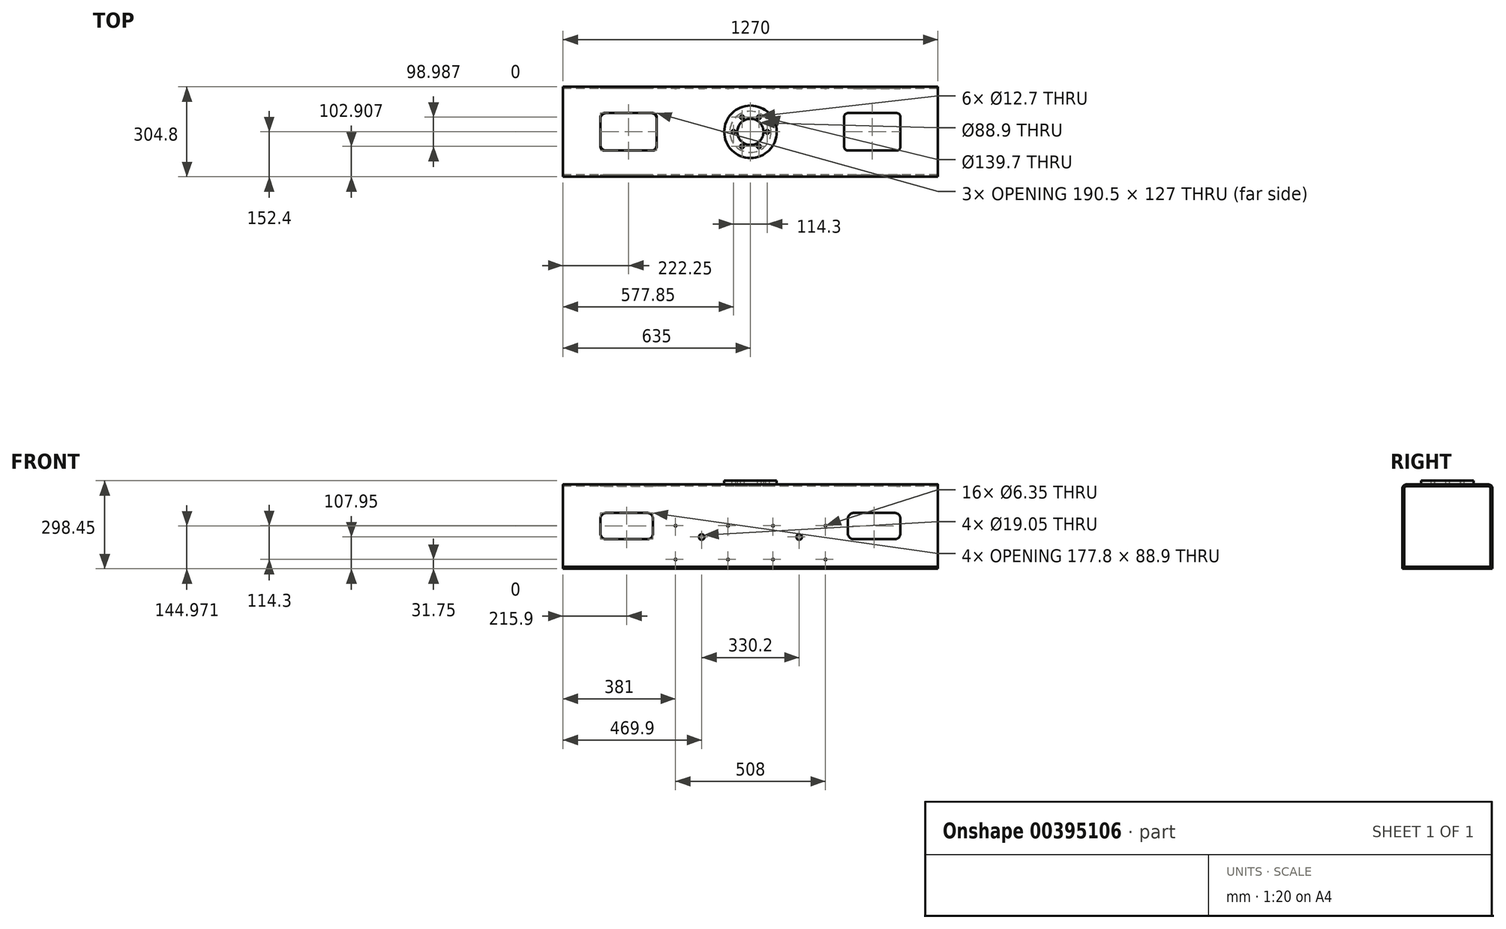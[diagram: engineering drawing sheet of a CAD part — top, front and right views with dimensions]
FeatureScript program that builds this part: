
annotation { "Feature Type Name" : "Feature", "Feature Type Description" : "" }
export const myFeature = defineFeature(function(context is Context, id is Id, definition is map)
    precondition{}
    {
        {
            var Q0;
            Q0=qCreatedBy(makeId("Right.planeOp"),FACE);
            var sketch = newSketch(context, id + "F0", { "sketchPlane" : qUnion([Q0])});
            skLineSegment(sketch, "E0.bottom", {"start": v(-139.7, 139.7) * mm, "end": v(139.7, 139.7) * mm});
            skLineSegment(sketch, "E0.top", {"start": v(-152.4, -139.7) * mm, "end": v(152.4, -139.7) * mm, "construction": true});
            skLineSegment(sketch, "E0.left", {"start": v(-152.4, 127) * mm, "end": v(-152.4, -139.7) * mm});
            skLineSegment(sketch, "E0.right", {"start": v(152.4, 127) * mm, "end": v(152.4, -139.7) * mm});
            skPoint(sketch, "E0.middle", {"position": v(0, 0) * mm});
            skLineSegment(sketch, "E1", {"start": v(-152.4, -139.7) * mm, "end": v(-146.05, -139.7) * mm});
            skLineSegment(sketch, "E2", {"start": v(146.05, -139.7) * mm, "end": v(152.4, -139.7) * mm});
            skPoint(sketch, "E3.visualSharp", {"position": v(-152.4, 139.7) * mm});
            skArc(sketch, "E3.filletArc", {"start": v(-139.7, 139.7) * mm, "mid": v(-148.68, 135.98) * mm, "end": v(-152.4, 127) * mm});
            skPoint(sketch, "E4.visualSharp", {"position": v(152.4, 139.7) * mm});
            skArc(sketch, "E4.filletArc", {"start": v(152.4, 127) * mm, "mid": v(148.68, 135.98) * mm, "end": v(139.7, 139.7) * mm});
            skLineSegment(sketch, "E5.0", {"start": v(-146.05, 127) * mm, "end": v(-146.05, -139.7) * mm});
            skArc(sketch, "E5.1", {"start": v(-139.7, 133.35) * mm, "mid": v(-144.2, 131.5) * mm, "end": v(-146.05, 127) * mm});
            skLineSegment(sketch, "E6.0", {"start": v(146.05, 127) * mm, "end": v(146.05, -139.7) * mm});
            skArc(sketch, "E6.1", {"start": v(146.05, 127) * mm, "mid": v(144.2, 131.5) * mm, "end": v(139.7, 133.35) * mm});
            skLineSegment(sketch, "E6.2", {"start": v(-139.7, 133.35) * mm, "end": v(139.7, 133.35) * mm});
            skSolve(sketch);
        }
        {
            var Q0;
            Q0 = qSketchRegion(id + "F0", true);
            extrude(context, id + "F1", {"entities" : qUnion([Q0]), "depth" : 1270 * mm});
        }
        {
            var Q0;
            Q0=makeQuery(id+"F1.opExtrude","SWEPT_FACE",FACE,{"disambiguationData":[OSD([sQuery(id+"F0.wireOp",EDGE,"E0.bottom")])]});
            var sketch = newSketch(context, id + "F2", { "sketchPlane" : qUnion([Q0])});
            skLineSegment(sketch, "E7", {"start": v(635, -139.7) * mm, "end": v(635, 139.7) * mm, "construction": true});
            skLineSegment(sketch, "E8.bottom", {"start": v(139.7, 63.5) * mm, "end": v(304.8, 63.5) * mm});
            skLineSegment(sketch, "E8.top", {"start": v(139.7, -63.5) * mm, "end": v(304.8, -63.5) * mm});
            skLineSegment(sketch, "E8.left", {"start": v(127, 50.8) * mm, "end": v(127, -50.8) * mm});
            skLineSegment(sketch, "E8.right", {"start": v(317.5, 50.8) * mm, "end": v(317.5, -50.8) * mm});
            skPoint(sketch, "E9.visualSharp", {"position": v(127, 63.5) * mm});
            skArc(sketch, "E9.filletArc", {"start": v(139.7, 63.5) * mm, "mid": v(130.72, 59.78) * mm, "end": v(127, 50.8) * mm});
            skPoint(sketch, "E10.visualSharp", {"position": v(317.5, 63.5) * mm});
            skArc(sketch, "E10.filletArc", {"start": v(317.5, 50.8) * mm, "mid": v(313.78, 59.78) * mm, "end": v(304.8, 63.5) * mm});
            skPoint(sketch, "E11.visualSharp", {"position": v(317.5, -63.5) * mm});
            skArc(sketch, "E11.filletArc", {"start": v(304.8, -63.5) * mm, "mid": v(313.78, -59.78) * mm, "end": v(317.5, -50.8) * mm});
            skPoint(sketch, "E12.visualSharp", {"position": v(127, -63.5) * mm});
            skArc(sketch, "E12.filletArc", {"start": v(127, -50.8) * mm, "mid": v(130.72, -59.78) * mm, "end": v(139.7, -63.5) * mm});
            skPoint(sketch, "E13.endSnap0", {"position": v(317.5, 0) * mm});
            skPoint(sketch, "E14.trimOffspring.end.orphan", {"position": v(3692.39, 0) * mm});
            skPoint(sketch, "E15.orphan", {"position": v(0, 0) * mm});
            skLineSegment(sketch, "E16.0", {"start": v(0, -139.7) * mm, "end": v(0, 139.7) * mm});
            skLineSegment(sketch, "E17.0", {"start": v(1270, -139.7) * mm, "end": v(1270, 139.7) * mm});
            skLineSegment(sketch, "E18", {"start": v(3692.39, 0) * mm, "end": v(0, 0) * mm, "construction": true});
            skPoint(sketch, "E19", {"position": v(127, 0) * mm});
            skLineSegment(sketch, "E20.MirrorCS", {"start": v(1130.3, -63.5) * mm, "end": v(965.2, -63.5) * mm});
            skArc(sketch, "E21.MirrorCS", {"start": v(965.2, -63.5) * mm, "mid": v(956.22, -59.78) * mm, "end": v(952.5, -50.8) * mm});
            skLineSegment(sketch, "E22.MirrorCS", {"start": v(952.5, 50.8) * mm, "end": v(952.5, -50.8) * mm});
            skArc(sketch, "E23.MirrorCS", {"start": v(952.5, 50.8) * mm, "mid": v(956.22, 59.78) * mm, "end": v(965.2, 63.5) * mm});
            skLineSegment(sketch, "E24.MirrorCS", {"start": v(1130.3, 63.5) * mm, "end": v(965.2, 63.5) * mm});
            skLineSegment(sketch, "E25.MirrorCS", {"start": v(1143, 50.8) * mm, "end": v(1143, -50.8) * mm});
            skArc(sketch, "E26.MirrorCS", {"start": v(1130.3, 63.5) * mm, "mid": v(1139.28, 59.78) * mm, "end": v(1143, 50.8) * mm});
            skArc(sketch, "E27.MirrorCS", {"start": v(1143, -50.8) * mm, "mid": v(1139.28, -59.78) * mm, "end": v(1130.3, -63.5) * mm});
            skCircle(sketch, "E28", {"center": v(635, 0) * mm, "radius": 69.85 * mm});
            skSolve(sketch);
        }
        {
            var Q0;
            Q0 = qSketchRegion(id + "F2", true);
            extrude(context, id + "F3", {"entities" : qUnion([Q0]), "operationType" : NewBodyOperationType.REMOVE, "endBound" : BoundingType.THROUGH_ALL, "oppositeDirection" : true, "depth" : 25.4 * mm});
        }
        {
            var Q0;
            Q0=makeQuery(id+"F1.opExtrude","SWEPT_FACE",FACE,{"disambiguationData":[OSD([sQuery(id+"F0.wireOp",EDGE,"E0.left")])]});
            var sketch = newSketch(context, id + "F4", { "sketchPlane" : qUnion([Q0])});
            skLineSegment(sketch, "E29", {"start": v(0, 0) * mm, "end": v(1270, -6.35) * mm, "construction": true});
            skLineSegment(sketch, "E30.bottom", {"start": v(146.05, 43.37) * mm, "end": v(285.75, 43.37) * mm});
            skLineSegment(sketch, "E30.top", {"start": v(146.05, -45.53) * mm, "end": v(285.75, -45.53) * mm});
            skLineSegment(sketch, "E30.left", {"start": v(127, 24.32) * mm, "end": v(127, -26.48) * mm});
            skLineSegment(sketch, "E30.right", {"start": v(304.8, 24.32) * mm, "end": v(304.8, -26.48) * mm});
            skPoint(sketch, "E30.middle", {"position": v(215.9, -1.08) * mm});
            skPoint(sketch, "E31.visualSharp", {"position": v(127, 43.37) * mm});
            skArc(sketch, "E31.filletArc", {"start": v(146.05, 43.37) * mm, "mid": v(132.58, 37.8) * mm, "end": v(127, 24.32) * mm});
            skPoint(sketch, "E32.visualSharp", {"position": v(304.8, 43.37) * mm});
            skArc(sketch, "E32.filletArc", {"start": v(304.8, 24.32) * mm, "mid": v(299.22, 37.8) * mm, "end": v(285.75, 43.37) * mm});
            skPoint(sketch, "E33.visualSharp", {"position": v(304.8, -45.53) * mm});
            skArc(sketch, "E33.filletArc", {"start": v(285.75, -45.53) * mm, "mid": v(299.22, -39.95) * mm, "end": v(304.8, -26.48) * mm});
            skPoint(sketch, "E34.visualSharp", {"position": v(127, -45.53) * mm});
            skArc(sketch, "E34.filletArc", {"start": v(127, -26.48) * mm, "mid": v(132.58, -39.95) * mm, "end": v(146.05, -45.53) * mm});
            skLineSegment(sketch, "E35", {"start": v(635, 127) * mm, "end": v(635, -139.7) * mm, "construction": true});
            skLineSegment(sketch, "E36.MirrorCS", {"start": v(1123.95, 43.37) * mm, "end": v(984.25, 43.37) * mm});
            skArc(sketch, "E37.MirrorCS", {"start": v(965.2, 24.32) * mm, "mid": v(970.78, 37.8) * mm, "end": v(984.25, 43.37) * mm});
            skLineSegment(sketch, "E38.MirrorCS", {"start": v(965.2, 24.32) * mm, "end": v(965.2, -26.48) * mm});
            skArc(sketch, "E39.MirrorCS", {"start": v(984.25, -45.53) * mm, "mid": v(970.78, -39.95) * mm, "end": v(965.2, -26.48) * mm});
            skLineSegment(sketch, "E40.MirrorCS", {"start": v(1123.95, -45.53) * mm, "end": v(984.25, -45.53) * mm});
            skArc(sketch, "E41.MirrorCS", {"start": v(1143, -26.48) * mm, "mid": v(1137.42, -39.95) * mm, "end": v(1123.95, -45.53) * mm});
            skArc(sketch, "E42.MirrorCS", {"start": v(1123.95, 43.37) * mm, "mid": v(1137.42, 37.8) * mm, "end": v(1143, 24.32) * mm});
            skLineSegment(sketch, "E43.MirrorCS", {"start": v(1143, 24.32) * mm, "end": v(1143, -26.48) * mm});
            skSolve(sketch);
        }
        {
            var Q0;
            Q0 = qSketchRegion(id + "F4", true);
            extrude(context, id + "F5", {"entities" : qUnion([Q0]), "operationType" : NewBodyOperationType.REMOVE, "endBound" : BoundingType.THROUGH_ALL, "oppositeDirection" : true, "depth" : 25.4 * mm});
        }
        {
            var Q0;
            Q0=makeQuery(id+"F1.opExtrude","SWEPT_FACE",FACE,{"disambiguationData":[OSD([sQuery(id+"F0.wireOp",EDGE,"E0.left")])]});
            var sketch = newSketch(context, id + "F6", { "sketchPlane" : qUnion([Q0])});
            skLineSegment(sketch, "E44", {"start": v(635, 127) * mm, "end": v(635, -139.7) * mm, "construction": true});
            skCircle(sketch, "E45", {"center": v(469.9, -38.1) * mm, "radius": 9.53 * mm});
            skCircle(sketch, "E46", {"center": v(558.8, 0) * mm, "radius": 3.17 * mm});
            skCircle(sketch, "E47.MirrorC", {"center": v(800.1, -38.1) * mm, "radius": 9.53 * mm});
            skCircle(sketch, "E48.MirrorC", {"center": v(711.2, 0) * mm, "radius": 3.17 * mm});
            skCircle(sketch, "E49", {"center": v(558.8, -114.3) * mm, "radius": 3.18 * mm});
            skCircle(sketch, "E50.MirrorC", {"center": v(711.2, -114.3) * mm, "radius": 3.18 * mm});
            skLineSegment(sketch, "E51", {"start": v(469.9, 31.48) * mm, "end": v(469.9, -139.7) * mm, "construction": true});
            skCircle(sketch, "E52.MirrorC", {"center": v(381, -114.3) * mm, "radius": 3.18 * mm});
            skCircle(sketch, "E53.MirrorC", {"center": v(381, 0) * mm, "radius": 3.17 * mm});
            skCircle(sketch, "E54.MirrorC", {"center": v(889, 0) * mm, "radius": 3.17 * mm});
            skCircle(sketch, "E55.MirrorC", {"center": v(889, -114.3) * mm, "radius": 3.18 * mm});
            skSolve(sketch);
        }
        {
            var Q0;
            Q0 = qSketchRegion(id + "F6", true);
            extrude(context, id + "F7", {"entities" : qUnion([Q0]), "operationType" : NewBodyOperationType.REMOVE, "endBound" : BoundingType.THROUGH_ALL, "oppositeDirection" : true, "depth" : 25.4 * mm});
        }
        {
            var Q0;
            Q0=makeQuery(id+"F1.opExtrude","SWEPT_FACE",FACE,{"disambiguationData":[OSD([sQuery(id+"F0.wireOp",EDGE,"E0.bottom")])]});
            var sketch = newSketch(context, id + "F8", { "sketchPlane" : qUnion([Q0])});
            skCircle(sketch, "E56.0", {"center": v(635, 0) * mm, "radius": 69.85 * mm, "construction": true});
            skCircle(sketch, "E57", {"center": v(635, 0) * mm, "radius": 88.9 * mm});
            skCircle(sketch, "E58", {"center": v(635, 0) * mm, "radius": 44.45 * mm});
            skCircle(sketch, "E59", {"center": v(577.85, 0) * mm, "radius": 6.35 * mm});
            skCircle(sketch, "E60.1.0", {"center": v(606.43, -49.5) * mm, "radius": 6.35 * mm});
            skCircle(sketch, "E60.2.0", {"center": v(663.58, -49.5) * mm, "radius": 6.35 * mm});
            skCircle(sketch, "E60.3.0", {"center": v(692.15, 0) * mm, "radius": 6.35 * mm});
            skCircle(sketch, "E60.4.0", {"center": v(663.58, 49.5) * mm, "radius": 6.35 * mm});
            skCircle(sketch, "E60.5.0", {"center": v(606.43, 49.5) * mm, "radius": 6.35 * mm});
            skSolve(sketch);
        }
        {
            var Q0;
            Q0 = qSketchRegion(id + "F8", true);
            extrude(context, id + "F9", {"entities" : qUnion([Q0]), "depth" : 12.7 * mm});
        }
        {
            var Q0;
            Q0=makeQuery(id+"F1.opExtrude","SWEPT_FACE",FACE,{"disambiguationData":[OSD([sQuery(id+"F0.wireOp",EDGE,"E1")])]});
            var sketch = newSketch(context, id + "F10", { "sketchPlane" : qUnion([Q0])});
            skLineSegment(sketch, "E61.0", {"start": v(1270, 152.4) * mm, "end": v(0, 152.4) * mm});
            skLineSegment(sketch, "E62.0", {"start": v(1270, -152.4) * mm, "end": v(0, -152.4) * mm});
            skPoint(sketch, "E63.0.end.orphan", {"position": v(0, 146.05) * mm});
            skPoint(sketch, "E63.0.start.orphan", {"position": v(1270, 146.05) * mm});
            skLineSegment(sketch, "E64", {"start": v(0, 152.4) * mm, "end": v(0, -152.4) * mm});
            skLineSegment(sketch, "E65", {"start": v(1270, 152.4) * mm, "end": v(1270, -152.4) * mm});
            skLineSegment(sketch, "E66", {"start": v(0, 0) * mm, "end": v(1270, 0) * mm, "construction": true});
            skLineSegment(sketch, "E67.bottom", {"start": v(146.05, 63.5) * mm, "end": v(298.45, 63.5) * mm});
            skLineSegment(sketch, "E67.top", {"start": v(146.05, -63.5) * mm, "end": v(298.45, -63.5) * mm});
            skLineSegment(sketch, "E67.left", {"start": v(127, 44.45) * mm, "end": v(127, -44.45) * mm});
            skLineSegment(sketch, "E67.right", {"start": v(317.5, 44.45) * mm, "end": v(317.5, -44.45) * mm});
            skPoint(sketch, "E67.middle", {"position": v(222.25, 0) * mm});
            skPoint(sketch, "E68.visualSharp", {"position": v(127, 63.5) * mm});
            skArc(sketch, "E68.filletArc", {"start": v(146.05, 63.5) * mm, "mid": v(132.58, 57.92) * mm, "end": v(127, 44.45) * mm});
            skPoint(sketch, "E69.visualSharp", {"position": v(317.5, 63.5) * mm});
            skArc(sketch, "E69.filletArc", {"start": v(317.5, 44.45) * mm, "mid": v(311.92, 57.92) * mm, "end": v(298.45, 63.5) * mm});
            skPoint(sketch, "E70.visualSharp", {"position": v(317.5, -63.5) * mm});
            skArc(sketch, "E70.filletArc", {"start": v(298.45, -63.5) * mm, "mid": v(311.92, -57.92) * mm, "end": v(317.5, -44.45) * mm});
            skPoint(sketch, "E71.visualSharp", {"position": v(127, -63.5) * mm});
            skArc(sketch, "E71.filletArc", {"start": v(127, -44.45) * mm, "mid": v(132.58, -57.92) * mm, "end": v(146.05, -63.5) * mm});
            skSolve(sketch);
        }
        {
            var Q0;
            Q0 = qSketchRegion(id + "F10", true);
            extrude(context, id + "F11", {"entities" : qUnion([Q0]), "depth" : 6.35 * mm});
        }
    });
